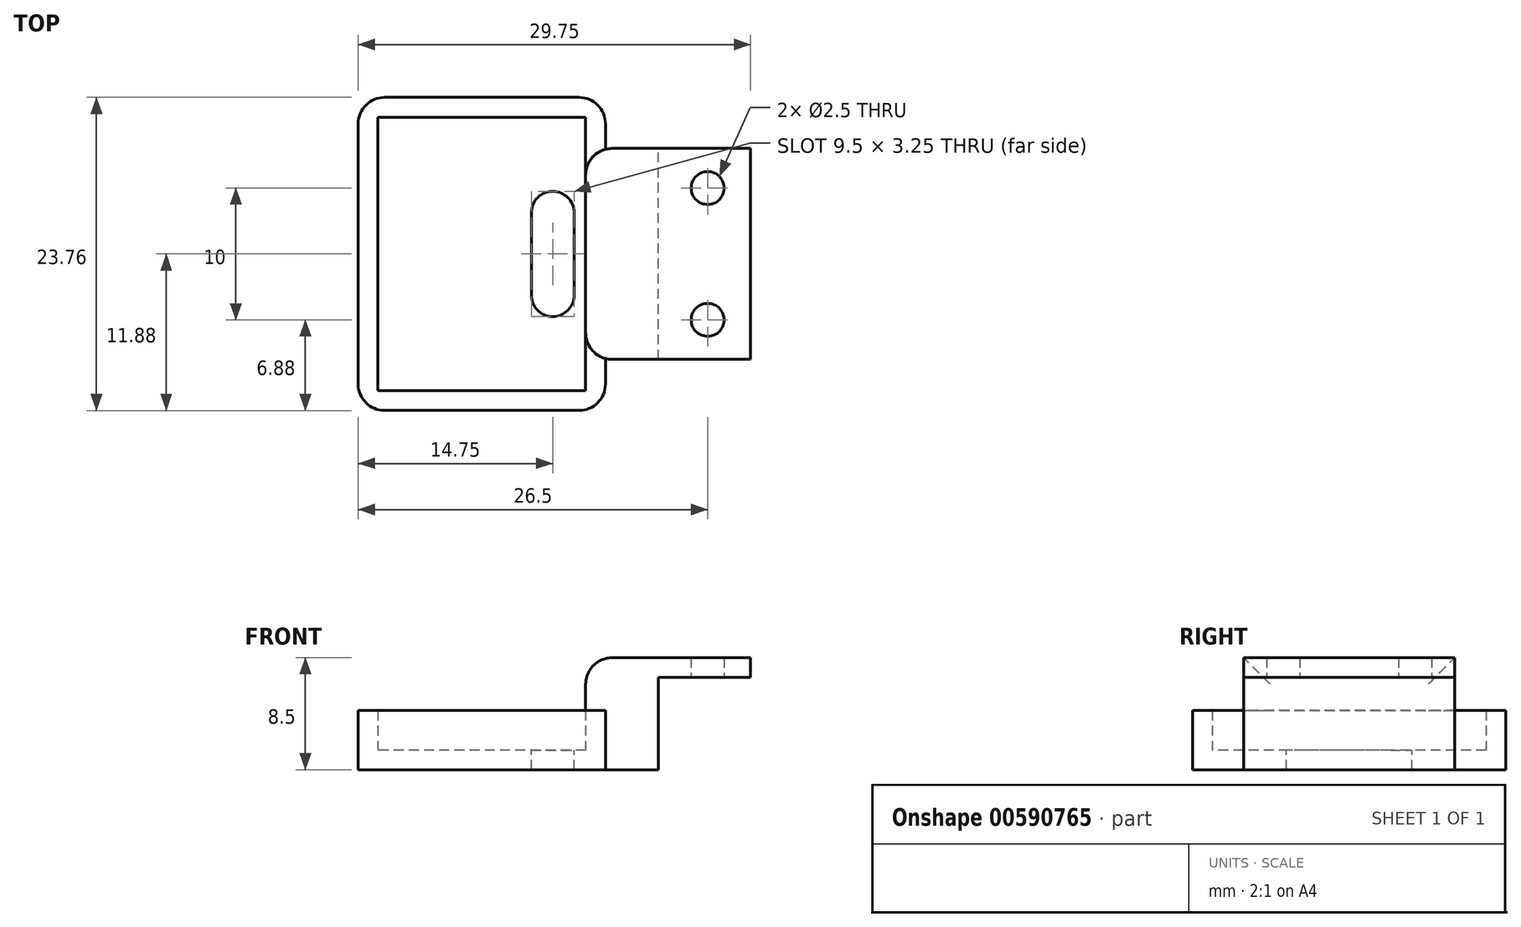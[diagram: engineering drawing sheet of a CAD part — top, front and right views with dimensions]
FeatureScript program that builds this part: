
annotation { "Feature Type Name" : "Feature", "Feature Type Description" : "" }
export const myFeature = defineFeature(function(context is Context, id is Id, definition is map)
    precondition{}
    {
        {
            var Q0;
            Q0=qCreatedBy(makeId("Top.planeOp"),FACE);
            var sketch = newSketch(context, id + "F0", { "sketchPlane" : qUnion([Q0])});
            skLineSegment(sketch, "E0.bottom", {"start": v(0, 0) * mm, "end": v(-12.5, 0) * mm});
            skLineSegment(sketch, "E0.top", {"start": v(0, -16) * mm, "end": v(-12.5, -16) * mm});
            skLineSegment(sketch, "E0.left", {"start": v(0, 0) * mm, "end": v(0, -16) * mm});
            skLineSegment(sketch, "E0.right", {"start": v(-12.5, 0) * mm, "end": v(-12.5, -16) * mm});
            skCircle(sketch, "E1", {"center": v(-3.25, -13) * mm, "radius": 1.25 * mm});
            skCircle(sketch, "E2", {"center": v(-3.25, -3) * mm, "radius": 1.25 * mm});
            skLineSegment(sketch, "E3", {"start": v(-3.25, -3) * mm, "end": v(-3.25, -13) * mm, "construction": true});
            skPoint(sketch, "E4", {"position": v(-3.25, -8) * mm});
            skPoint(sketch, "E5", {"position": v(0, -8) * mm});
            skSolve(sketch);
        }
        {
            var Q0;
            Q0=makeQuery(id+"F0.imprint","IMPRINT",FACE,{"disambiguationData":[TD([[makeQuery(id+"F0.imprint","IMPRINT",EDGE,{"derivedFrom":sQuery(id+"F0.wireOp",EDGE,"E0.bottom")}),1.0]])]});
            extrude(context, id + "F1", {"entities" : qUnion([Q0]), "depth" : 1.5 * mm, "offsetDistance" : 25 * mm});
        }
        {
            var Q0;
            Q0=makeQuery(id+"F1.opExtrude","CAP_FACE",FACE,{"disambiguationData":[OSD([sQuery(id+"F0.wireOp",EDGE,"E0.bottom"),sQuery(id+"F0.wireOp",EDGE,"E0.top"),sQuery(id+"F0.wireOp",EDGE,"E0.left"),sQuery(id+"F0.wireOp",EDGE,"E0.right"),sQuery(id+"F0.wireOp",EDGE,"E1"),sQuery(id+"F0.wireOp",EDGE,"E2")])],"isStart":true});
            var sketch = newSketch(context, id + "F2", { "sketchPlane" : qUnion([Q0])});
            skLineSegment(sketch, "E6.bottom", {"start": v(-12.5, 16) * mm, "end": v(-11, 16) * mm});
            skLineSegment(sketch, "E6.top", {"start": v(-12.5, 0) * mm, "end": v(-11, 0) * mm});
            skLineSegment(sketch, "E6.left", {"start": v(-12.5, 16) * mm, "end": v(-12.5, 0) * mm});
            skLineSegment(sketch, "E6.right", {"start": v(-11, 16) * mm, "end": v(-11, 0) * mm});
            skSolve(sketch);
        }
        {
            var Q0;
            Q0=makeQuery(id+"F2.imprint","IMPRINT",FACE,{"disambiguationData":[TD([[makeQuery(id+"F2.imprint","IMPRINT",EDGE,{"derivedFrom":sQuery(id+"F2.wireOp",EDGE,"E6.bottom")}),1.0]])]});
            extrude(context, id + "F3", {"entities" : qUnion([Q0]), "operationType" : NewBodyOperationType.ADD, "depth" : 5.5 * mm, "offsetDistance" : 25 * mm});
        }
        {
            var Q0;
            Q0=makeQuery(id+"F3.opExtrude","CAP_FACE",FACE,{"disambiguationData":[OSD([sQuery(id+"F2.wireOp",EDGE,"E6.bottom"),sQuery(id+"F2.wireOp",EDGE,"E6.top"),sQuery(id+"F2.wireOp",EDGE,"E6.left"),sQuery(id+"F2.wireOp",EDGE,"E6.right")])],"isStart":false});
            var sketch = newSketch(context, id + "F4", { "sketchPlane" : qUnion([Q0])});
            skLineSegment(sketch, "E7.bottom", {"start": v(-11, 19.87) * mm, "end": v(-29.75, 19.87) * mm});
            skLineSegment(sketch, "E7.top", {"start": v(-11, -3.87) * mm, "end": v(-29.75, -3.87) * mm});
            skLineSegment(sketch, "E7.left", {"start": v(-11, 19.87) * mm, "end": v(-11, -3.87) * mm});
            skLineSegment(sketch, "E7.right", {"start": v(-29.75, 19.87) * mm, "end": v(-29.75, -3.87) * mm});
            skPoint(sketch, "E8", {"position": v(-11, 8) * mm});
            skLineSegment(sketch, "E9", {"start": v(-12.5, 16) * mm, "end": v(-12.5, 0) * mm});
            skLineSegment(sketch, "E10", {"start": v(-12.5, 0) * mm, "end": v(-12.5, -2.37) * mm});
            skLineSegment(sketch, "E11", {"start": v(-12.5, -2.37) * mm, "end": v(-28.25, -2.37) * mm});
            skLineSegment(sketch, "E12", {"start": v(-28.25, -2.37) * mm, "end": v(-28.25, 18.38) * mm});
            skLineSegment(sketch, "E13", {"start": v(-28.25, 18.38) * mm, "end": v(-12.5, 18.38) * mm});
            skLineSegment(sketch, "E14", {"start": v(-12.5, 18.38) * mm, "end": v(-12.5, 16) * mm});
            skLineSegment(sketch, "E15", {"start": v(-13.38, 4.88) * mm, "end": v(-13.38, 11.12) * mm});
            skLineSegment(sketch, "E16", {"start": v(-16.62, 4.88) * mm, "end": v(-16.62, 11.12) * mm});
            skArc(sketch, "E17", {"start": v(-16.62, 4.88) * mm, "mid": v(-15, 3.25) * mm, "end": v(-13.38, 4.88) * mm});
            skArc(sketch, "E18", {"start": v(-13.38, 11.12) * mm, "mid": v(-15, 12.75) * mm, "end": v(-16.62, 11.12) * mm});
            skPoint(sketch, "E19", {"position": v(-13.38, 8) * mm});
            skSolve(sketch);
        }
        {
            var Q0;
            {var subQ0=sQuery(id+"F4.wireOp",EDGE,"E7.bottom");Q0=makeQuery(id+"F4.imprint","IMPRINT",FACE,{"disambiguationData":[TD([[makeQuery(id+"F4.imprint","IMPRINT",EDGE,{"derivedFrom":subQ0}),1.0]])]});}
            extrude(context, id + "F5", {"entities" : qUnion([Q0]), "operationType" : NewBodyOperationType.ADD, "oppositeDirection" : true, "depth" : 3 * mm, "offsetDistance" : 25 * mm});
        }
        {
            var Q0;
            Q0=qSketchRegion(id+"F4",true);
            var Q1;
            Q1=makeQuery(id+"F4.imprint","IMPRINT",FACE,{"disambiguationData":[TD([[makeQuery(id+"F4.imprint","IMPRINT",EDGE,{"derivedFrom":sQuery(id+"F4.wireOp",EDGE,"E9")}),1.0]])]});
            extrude(context, id + "F6", {"entities" : qUnion([Q0, Q1]), "operationType" : NewBodyOperationType.ADD, "depth" : 1.5 * mm, "offsetDistance" : 25 * mm});
        }
        {
            var Q0;
            {var subQ0=sQuery(id+"F4.wireOp",EDGE,"E7.left");Q0=makeQuery(id+"F6.boolean.opBoolean","MERGE",FACE,{"derivedFrom":[makeQuery(id+"F5.boolean.opBoolean","MERGE",FACE,{"derivedFrom":[makeQuery(id+"F3.opExtrude","SWEPT_FACE",FACE,{"disambiguationData":[OSD([sQuery(id+"F2.wireOp",EDGE,"E6.right")])]}),makeQuery(id+"F5.opExtrude","SWEPT_FACE",FACE,{"disambiguationData":[OSD([subQ0]),TDD([makeQuery(id+"F4.imprint","IMPRINT",EDGE,{"disambiguationData":[TD([[makeQuery(id+"F4.imprint","INTERSECT",VERTEX,{"derivedFrom":[makeQuery(id+"F3.opExtrude","CAP_EDGE",EDGE,{"disambiguationData":[OSD([sQuery(id+"F2.wireOp",EDGE,"E6.bottom")])],"isStart":false}),subQ0]}),1.0]])],"derivedFrom":subQ0})])]}),makeQuery(id+"F5.opExtrude","SWEPT_FACE",FACE,{"disambiguationData":[OSD([subQ0]),TDD([makeQuery(id+"F4.imprint","IMPRINT",EDGE,{"disambiguationData":[TD([[makeQuery(id+"F4.imprint","INTERSECT",VERTEX,{"derivedFrom":[makeQuery(id+"F3.opExtrude","CAP_EDGE",EDGE,{"disambiguationData":[OSD([sQuery(id+"F2.wireOp",EDGE,"E6.top")])],"isStart":false}),subQ0]}),-1.0]])],"derivedFrom":subQ0})])]})]}),makeQuery(id+"F6.opExtrude","SWEPT_FACE",FACE,{"disambiguationData":[OSD([subQ0])]})]});}
            var sketch = newSketch(context, id + "F7", { "sketchPlane" : qUnion([Q0])});
            skLineSegment(sketch, "E20.bottom", {"start": v(-16, 0) * mm, "end": v(0, 0) * mm});
            skLineSegment(sketch, "E20.top", {"start": v(-16, -7) * mm, "end": v(0, -7) * mm});
            skLineSegment(sketch, "E20.left", {"start": v(-16, 0) * mm, "end": v(-16, -7) * mm});
            skLineSegment(sketch, "E20.right", {"start": v(0, 0) * mm, "end": v(0, -7) * mm});
            skSolve(sketch);
        }
        {
            var Q0;
            {var subQ1=sQuery(id+"F7.wireOp",EDGE,"E20.bottom");Q0=makeQuery(id+"F7.imprint","IMPRINT",FACE,{"disambiguationData":[TD([[makeQuery(id+"F7.imprint","IMPRINT",EDGE,{"derivedFrom":subQ1}),-1.0]])]});}
            extrude(context, id + "F8", {"entities" : qUnion([Q0]), "operationType" : NewBodyOperationType.ADD, "depth" : 4 * mm, "offsetDistance" : 25 * mm});
        }
        {
            var Q0;
            {var subQ0=sQuery(id+"F4.wireOp",EDGE,"E7.right");var subQ1=sQuery(id+"F4.wireOp",EDGE,"E7.top");Q0=makeQuery(id+"F6.boolean.opBoolean","MERGE",EDGE,{"derivedFrom":[makeQuery(id+"F5.opExtrude","SWEPT_EDGE",EDGE,{"disambiguationData":[OSD([subQ1,subQ0])]}),makeQuery(id+"F6.opExtrude","SWEPT_EDGE",EDGE,{"disambiguationData":[OSD([subQ1,subQ0])]})]});}
            var Q1;
            {var subQ0=sQuery(id+"F4.wireOp",EDGE,"E7.right");var subQ1=sQuery(id+"F4.wireOp",EDGE,"E7.bottom");Q1=makeQuery(id+"F6.boolean.opBoolean","MERGE",EDGE,{"derivedFrom":[makeQuery(id+"F5.opExtrude","SWEPT_EDGE",EDGE,{"disambiguationData":[OSD([subQ1,subQ0])]}),makeQuery(id+"F6.opExtrude","SWEPT_EDGE",EDGE,{"disambiguationData":[OSD([subQ1,subQ0])]})]});}
            var Q2;
            {var subQ0=sQuery(id+"F4.wireOp",EDGE,"E7.left");var subQ1=sQuery(id+"F4.wireOp",EDGE,"E7.bottom");Q2=makeQuery(id+"F6.boolean.opBoolean","MERGE",EDGE,{"derivedFrom":[makeQuery(id+"F5.opExtrude","SWEPT_EDGE",EDGE,{"disambiguationData":[OSD([subQ1,subQ0])]}),makeQuery(id+"F6.opExtrude","SWEPT_EDGE",EDGE,{"disambiguationData":[OSD([subQ1,subQ0])]})]});}
            var Q3;
            {var subQ0=sQuery(id+"F4.wireOp",EDGE,"E7.left");var subQ1=sQuery(id+"F4.wireOp",EDGE,"E7.top");Q3=makeQuery(id+"F6.boolean.opBoolean","MERGE",EDGE,{"derivedFrom":[makeQuery(id+"F5.opExtrude","SWEPT_EDGE",EDGE,{"disambiguationData":[OSD([subQ1,subQ0])]}),makeQuery(id+"F6.opExtrude","SWEPT_EDGE",EDGE,{"disambiguationData":[OSD([subQ1,subQ0])]})]});}
            var Q4;
            Q4=makeQuery(id+"F1.opExtrude","CAP_EDGE",EDGE,{"disambiguationData":[OSD([sQuery(id+"F0.wireOp",EDGE,"E0.right")])],"isStart":false});
            var Q5;
            Q5=makeQuery(id+"F3.boolean.opBoolean","MERGE",EDGE,{"derivedFrom":[makeQuery(id+"F1.opExtrude","SWEPT_EDGE",EDGE,{"disambiguationData":[OSD([sQuery(id+"F0.wireOp",EDGE,"E0.top"),sQuery(id+"F0.wireOp",EDGE,"E0.right")])]}),makeQuery(id+"F3.opExtrude","SWEPT_EDGE",EDGE,{"disambiguationData":[OSD([sQuery(id+"F2.wireOp",EDGE,"E6.bottom"),sQuery(id+"F2.wireOp",EDGE,"E6.left")])]})]});
            var Q6;
            Q6=makeQuery(id+"F3.boolean.opBoolean","MERGE",EDGE,{"derivedFrom":[makeQuery(id+"F1.opExtrude","SWEPT_EDGE",EDGE,{"disambiguationData":[OSD([sQuery(id+"F0.wireOp",EDGE,"E0.bottom"),sQuery(id+"F0.wireOp",EDGE,"E0.right")])]}),makeQuery(id+"F3.opExtrude","SWEPT_EDGE",EDGE,{"disambiguationData":[OSD([sQuery(id+"F2.wireOp",EDGE,"E6.top"),sQuery(id+"F2.wireOp",EDGE,"E6.left")])]})]});
            fillet(context, id + "F9", {"entities" : qUnion([Q0, Q1, Q2, Q3, Q4, Q5, Q6]), "radius" : 2 * mm, "tangentPropagation" : true, "allowEdgeOverflow" : false});
        }
    });
